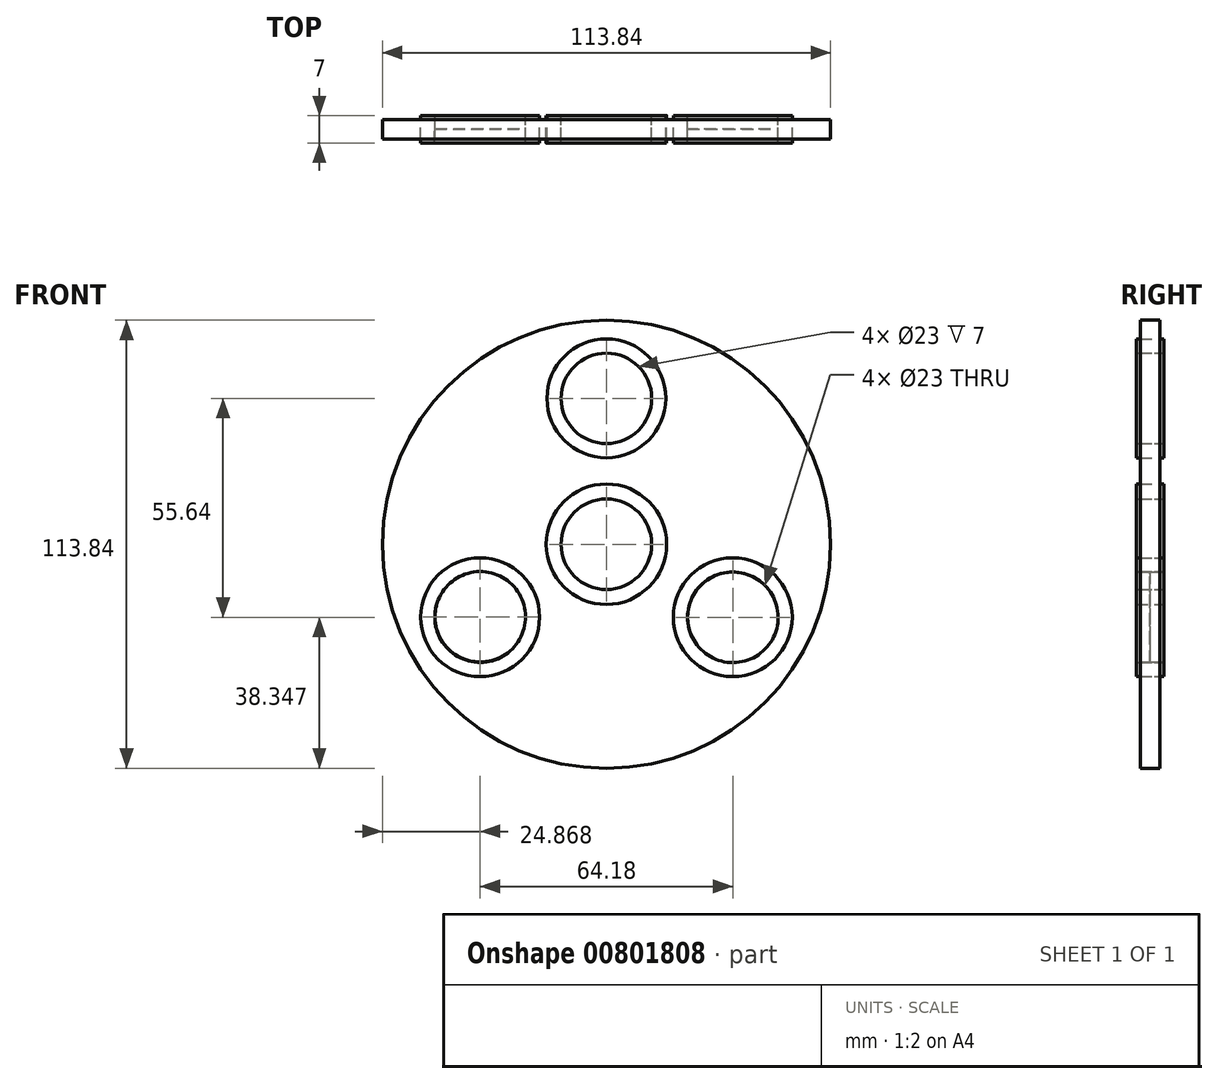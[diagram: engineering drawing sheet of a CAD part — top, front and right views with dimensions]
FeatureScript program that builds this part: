
annotation { "Feature Type Name" : "Feature", "Feature Type Description" : "" }
export const myFeature = defineFeature(function(context is Context, id is Id, definition is map)
    precondition{}
    {
        {
            var Q0;
            Q0=qCreatedBy(makeId("Front.planeOp"),FACE);
            var sketch = newSketch(context, id + "F0", { "sketchPlane" : qUnion([Q0])});
            skCircle(sketch, "E0", {"center": v(0, 0) * mm, "radius": 11.16 * mm});
            skCircle(sketch, "E1", {"center": v(0, 0) * mm, "radius": 15.3 * mm});
            skSolve(sketch);
        }
        {
            var Q0;
            Q0=makeQuery(id+"F0.imprint","IMPRINT",FACE,{"disambiguationData":[TD([[makeQuery(id+"F0.imprint","IMPRINT",EDGE,{"derivedFrom":sQuery(id+"F0.wireOp",EDGE,"E0")}),-1.0]])]});
            extrude(context, id + "F1", {"entities" : qUnion([Q0]), "endBound" : BoundingType.SYMMETRIC, "depth" : 7 * mm, "offsetDistance" : 25 * mm});
        }
        {
            var Q0;
            Q0=qCreatedBy(makeId("Front.planeOp"),FACE);
            var sketch = newSketch(context, id + "F2", { "sketchPlane" : qUnion([Q0])});
            skCircle(sketch, "E2", {"center": v(0, 37.07) * mm, "radius": 11.37 * mm});
            skCircle(sketch, "E3", {"center": v(0, 37.07) * mm, "radius": 15.1 * mm});
            skSolve(sketch);
        }
        {
            var Q0;
            Q0=makeQuery(id+"F2.imprint","IMPRINT",FACE,{"disambiguationData":[TD([[makeQuery(id+"F2.imprint","IMPRINT",EDGE,{"derivedFrom":sQuery(id+"F2.wireOp",EDGE,"E2")}),-1.0]])]});
            extrude(context, id + "F3", {"entities" : qUnion([Q0]), "endBound" : BoundingType.SYMMETRIC, "depth" : 7 * mm, "offsetDistance" : 25 * mm});
        }
        {
            var Q0;
            Q0=sQuery(id+"F2.wireOp",VERTEX,"E2.center");
            var Q1;
            Q1=sQuery(id+"F0.wireOp",VERTEX,"E0.center");
            var Q2;
            Q2=sQuery(id+"FDXTKNDJFSV6p6a_2.wireOp",VERTEX,"iIKWwuOU-dUiv-7WZT-DDIS-tuBt11lw8FF3.center");
            var Q3;
            Q3=sQuery(id+"FdeEN6DHI3HbTYX_3.wireOp",VERTEX,"QeM9H9HY-sM6H-ASrl-pTQM-CbxIrUDouZmM.center");
            var Q4;
            Q4=makeQuery(id+"F3.opExtrude","SWEPT_BODY",BODY,{"disambiguationData":[OSD([sQuery(id+"F2.wireOp",EDGE,"E2"),sQuery(id+"F2.wireOp",EDGE,"E3")])]});
            var Q5;
            Q5=makeQuery(id+"FTqENTmPFNy3YpX_4.opExtrude","SWEPT_BODY",BODY,{"disambiguationData":[OSD([sQuery(id+"FhGpq1EQWEpvfbD_4.wireOp",EDGE,"InvaKnHi-rKI6-r932-Zz3O-strSpI5VSyeA")])]});
            var Q6;
            Q6=makeQuery(id+"F1.opExtrude","SWEPT_BODY",BODY,{"disambiguationData":[OSD([sQuery(id+"F0.wireOp",EDGE,"E0"),sQuery(id+"F0.wireOp",EDGE,"E1")])]});
            var Q7;
            Q7=makeQuery(id+"F1N4JzOER8HhmVg_2.opExtrude","SWEPT_BODY",BODY,{"disambiguationData":[OSD([sQuery(id+"FDXTKNDJFSV6p6a_2.wireOp",EDGE,"iIKWwuOU-dUiv-7WZT-DDIS-tuBt11lw8FF3"),sQuery(id+"FDXTKNDJFSV6p6a_2.wireOp",EDGE,"TxBW1mjY-K2RO-JvZw-DXNG-JuuVmlftTWbc")])]});
            var Q8;
            Q8=makeQuery(id+"FyTJGoQFqu1NP7b_3.opExtrude","SWEPT_BODY",BODY,{"disambiguationData":[OSD([sQuery(id+"FdeEN6DHI3HbTYX_3.wireOp",EDGE,"QeM9H9HY-sM6H-ASrl-pTQM-CbxIrUDouZmM"),sQuery(id+"FdeEN6DHI3HbTYX_3.wireOp",EDGE,"oHU4NrP5-JlVZ-CuUB-y5kG-UOjHcyC3QuUe")])]});
            hole(context, id + "F4", {"style" : HoleStyle.SIMPLE, "endStyle" : HoleEndStyle.THROUGH, "oppositeDirection" : true, "holeDiameter" : 23 * mm, "majorDiameter" : 5 * mm, "isTappedThrough" : true, "tappedDepth" : 12 * mm, "tapClearance" : 3, "locations" : qUnion([Q0, Q1, Q2, Q3]), "scope" : qUnion([Q4, Q5, Q6, Q7, Q8])});
        }
        {
            var Q0;
            Q0=makeQuery(id+"F3.opExtrude","SWEPT_BODY",BODY,{"disambiguationData":[OSD([sQuery(id+"F2.wireOp",EDGE,"E2"),sQuery(id+"F2.wireOp",EDGE,"E3")])]});
            var Q1;
            Q1=sQuery(id+"F0.wireOp",EDGE,"E0");
            circularPattern(context, id + "F5", {"entities" : qUnion([Q0]), "axis" : qUnion([Q1]), "angle" : 360 * degree, "instanceCount" : 3, "equalSpace" : true});
        }
        {
            var Q0;
            Q0=qCreatedBy(makeId("Front.planeOp"),FACE);
            var sketch = newSketch(context, id + "F6", { "sketchPlane" : qUnion([Q0])});
            skCircle(sketch, "E4", {"center": v(0, 0) * mm, "radius": 56.92 * mm});
            skSolve(sketch);
        }
        {
            var Q0;
            Q0=makeQuery(id+"F6.imprint","IMPRINT",FACE,{"disambiguationData":[TD([[makeQuery(id+"F6.imprint","IMPRINT",EDGE,{"derivedFrom":sQuery(id+"F6.wireOp",EDGE,"E4")}),1.0]])]});
            extrude(context, id + "F7", {"entities" : qUnion([Q0]), "endBound" : BoundingType.SYMMETRIC, "depth" : 5 * mm, "offsetDistance" : 25 * mm});
        }
        {
            var Q0;
            Q0=qCreatedBy(makeId("Front.planeOp"),FACE);
            var sketch = newSketch(context, id + "F8", { "sketchPlane" : qUnion([Q0])});
            skCircle(sketch, "E5", {"center": v(32.13, -18.57) * mm, "radius": 11.63 * mm});
            skSolve(sketch);
        }
        {
            var Q0;
            Q0=sQuery(id+"F8.wireOp",VERTEX,"E5.center");
            var Q1;
            Q1=sQuery(id+"F0.wireOp",VERTEX,"E0.center");
            var Q2;
            Q2=sQuery(id+"F2.wireOp",VERTEX,"E2.center");
            var Q3;
            Q3=makeQuery(id+"F5.opPattern","COPY",BODY,{"derivedFrom":makeQuery(id+"F3.opExtrude","SWEPT_BODY",BODY,{"disambiguationData":[OSD([sQuery(id+"F2.wireOp",EDGE,"E2"),sQuery(id+"F2.wireOp",EDGE,"E3")])]}),"instanceName":"2"});
            var Q4;
            Q4=makeQuery(id+"F7.opExtrude","SWEPT_BODY",BODY,{"disambiguationData":[OSD([sQuery(id+"F6.wireOp",EDGE,"E4")])]});
            hole(context, id + "F9", {"style" : HoleStyle.SIMPLE, "endStyle" : HoleEndStyle.THROUGH, "oppositeDirection" : true, "holeDiameter" : 23 * mm, "majorDiameter" : 5 * mm, "isTappedThrough" : true, "tappedDepth" : 12 * mm, "tapClearance" : 3, "locations" : qUnion([Q0, Q1, Q2]), "scope" : qUnion([Q3, Q4])});
        }
        {
            var Q0;
            Q0=qCreatedBy(makeId("Front.planeOp"),FACE);
            var sketch = newSketch(context, id + "F10", { "sketchPlane" : qUnion([Q0])});
            skCircle(sketch, "E6", {"center": v(-32.05, -18.45) * mm, "radius": 11.44 * mm});
            skSolve(sketch);
        }
        {
            var Q0;
            Q0=sQuery(id+"F10.wireOp",VERTEX,"E6.center");
            var Q1;
            Q1=makeQuery(id+"F7.opExtrude","SWEPT_BODY",BODY,{"disambiguationData":[OSD([sQuery(id+"F6.wireOp",EDGE,"E4")])]});
            var Q2;
            Q2=makeQuery(id+"F5.opPattern","COPY",BODY,{"derivedFrom":makeQuery(id+"F3.opExtrude","SWEPT_BODY",BODY,{"disambiguationData":[OSD([sQuery(id+"F2.wireOp",EDGE,"E2"),sQuery(id+"F2.wireOp",EDGE,"E3")])]}),"instanceName":"1"});
            hole(context, id + "F11", {"style" : HoleStyle.SIMPLE, "endStyle" : HoleEndStyle.THROUGH, "oppositeDirection" : true, "holeDiameter" : 23 * mm, "majorDiameter" : 5 * mm, "isTappedThrough" : true, "tappedDepth" : 12 * mm, "tapClearance" : 3, "locations" : qUnion([Q0]), "scope" : qUnion([Q1, Q2])});
        }
        {
            var Q0;
            Q0=sQuery(id+"F2.wireOp",VERTEX,"E2.center");
            var Q1;
            Q1=sQuery(id+"F0.wireOp",VERTEX,"E0.center");
            var Q2;
            Q2=sQuery(id+"F10.wireOp",VERTEX,"E6.center");
            var Q3;
            Q3=sQuery(id+"F8.wireOp",VERTEX,"E5.center");
            var Q4;
            Q4=makeQuery(id+"F1.opExtrude","SWEPT_BODY",BODY,{"disambiguationData":[OSD([sQuery(id+"F0.wireOp",EDGE,"E0"),sQuery(id+"F0.wireOp",EDGE,"E1")])]});
            var Q5;
            Q5=makeQuery(id+"F3.opExtrude","SWEPT_BODY",BODY,{"disambiguationData":[OSD([sQuery(id+"F2.wireOp",EDGE,"E2"),sQuery(id+"F2.wireOp",EDGE,"E3")])]});
            var Q6;
            Q6=makeQuery(id+"F5.opPattern","COPY",BODY,{"derivedFrom":makeQuery(id+"F3.opExtrude","SWEPT_BODY",BODY,{"disambiguationData":[OSD([sQuery(id+"F2.wireOp",EDGE,"E2"),sQuery(id+"F2.wireOp",EDGE,"E3")])]}),"instanceName":"2"});
            var Q7;
            Q7=makeQuery(id+"F7.opExtrude","SWEPT_BODY",BODY,{"disambiguationData":[OSD([sQuery(id+"F6.wireOp",EDGE,"E4")])]});
            var Q8;
            Q8=makeQuery(id+"F5.opPattern","COPY",BODY,{"derivedFrom":makeQuery(id+"F3.opExtrude","SWEPT_BODY",BODY,{"disambiguationData":[OSD([sQuery(id+"F2.wireOp",EDGE,"E2"),sQuery(id+"F2.wireOp",EDGE,"E3")])]}),"instanceName":"1"});
            hole(context, id + "F12", {"style" : HoleStyle.SIMPLE, "endStyle" : HoleEndStyle.THROUGH, "holeDiameter" : 23 * mm, "majorDiameter" : 5 * mm, "isTappedThrough" : true, "tappedDepth" : 12 * mm, "tapClearance" : 3, "locations" : qUnion([Q0, Q1, Q2, Q3]), "scope" : qUnion([Q4, Q5, Q6, Q7, Q8])});
        }
    });
